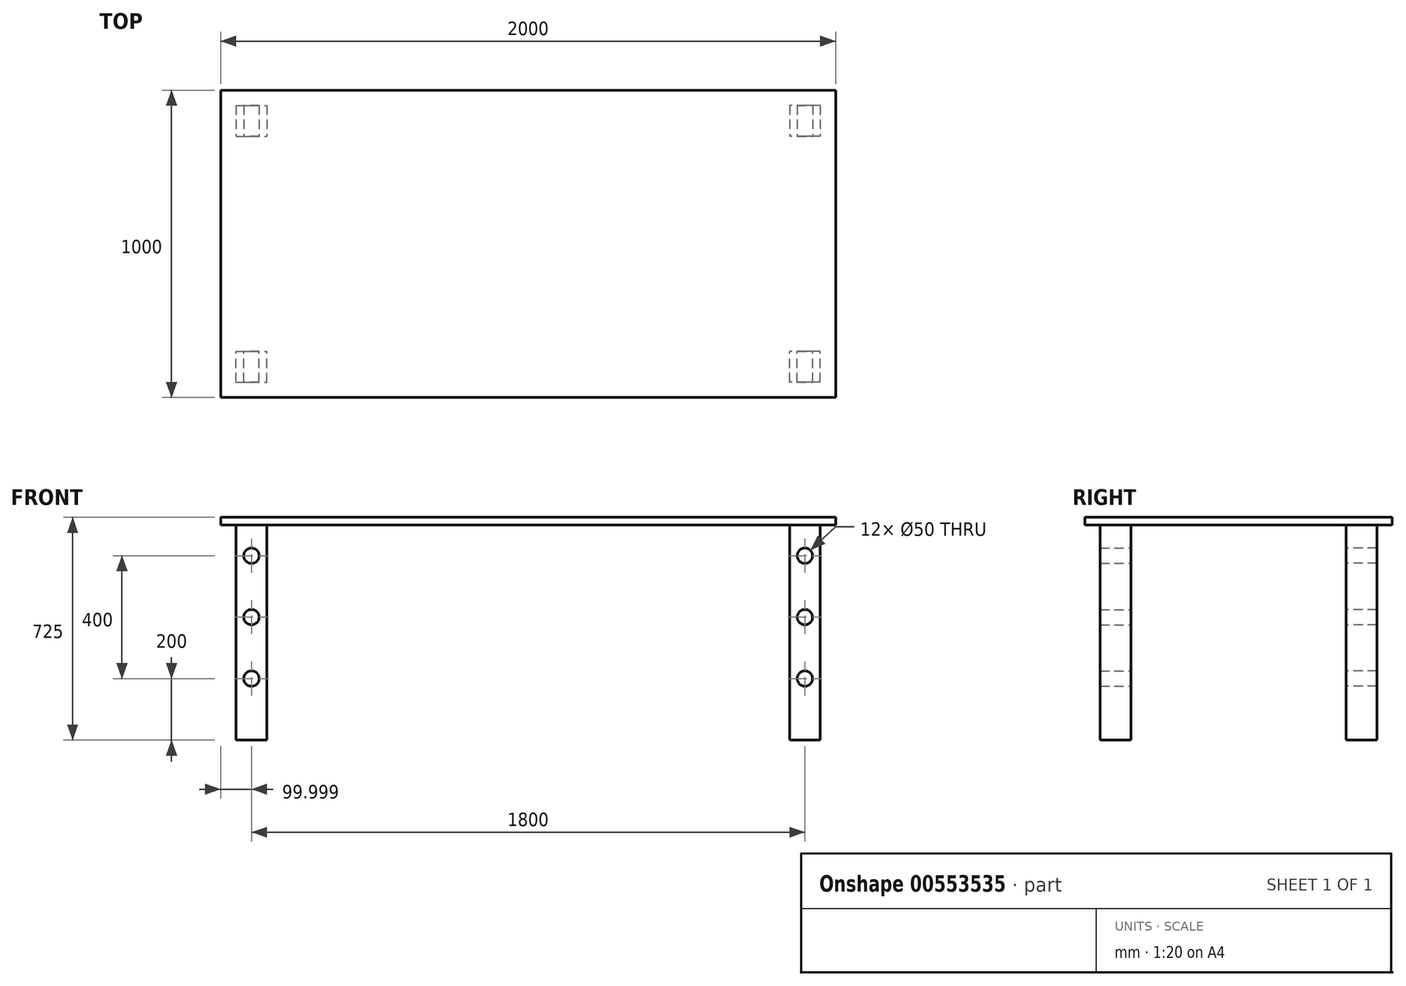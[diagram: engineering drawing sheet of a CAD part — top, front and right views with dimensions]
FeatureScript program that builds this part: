
annotation { "Feature Type Name" : "Feature", "Feature Type Description" : "" }
export const myFeature = defineFeature(function(context is Context, id is Id, definition is map)
    precondition{}
    {
        {
            var Q0;
            Q0=qCreatedBy(makeId("Top.planeOp"),FACE);
            var sketch = newSketch(context, id + "F0", { "sketchPlane" : qUnion([Q0])});
            skLineSegment(sketch, "E0.bottom", {"start": v(-581.73, 260.2) * mm, "end": v(418.27, 260.2) * mm});
            skLineSegment(sketch, "E0.top", {"start": v(-581.73, -239.8) * mm, "end": v(418.27, -239.8) * mm});
            skLineSegment(sketch, "E0.left", {"start": v(-581.73, 260.2) * mm, "end": v(-581.73, -239.8) * mm});
            skLineSegment(sketch, "E0.right", {"start": v(418.27, 260.2) * mm, "end": v(418.27, -239.8) * mm});
            skLineSegment(sketch, "E1.bottom", {"start": v(-531.73, 210.2) * mm, "end": v(-431.73, 210.2) * mm});
            skLineSegment(sketch, "E1.top", {"start": v(-531.73, 110.2) * mm, "end": v(-431.73, 110.2) * mm});
            skLineSegment(sketch, "E1.left", {"start": v(-531.73, 210.2) * mm, "end": v(-531.73, 110.2) * mm});
            skLineSegment(sketch, "E1.right", {"start": v(-431.73, 210.2) * mm, "end": v(-431.73, 110.2) * mm});
            skSolve(sketch);
        }
        {
            var Q0;
            Q0=makeQuery(id+"F0.imprint","IMPRINT",FACE,{"disambiguationData":[TD([[makeQuery(id+"F0.imprint","IMPRINT",EDGE,{"derivedFrom":sQuery(id+"F0.wireOp",EDGE,"E1.bottom")}),-1.0]])]});
            var Q1;
            Q1=makeQuery(id+"F0.imprint","IMPRINT",FACE,{"disambiguationData":[TD([[makeQuery(id+"F0.imprint","IMPRINT",EDGE,{"derivedFrom":sQuery(id+"F0.wireOp",EDGE,"E0.bottom")}),-1.0]])]});
            extrude(context, id + "F1", {"entities" : qUnion([Q0, Q1]), "depth" : 25 * mm, "offsetDistance" : 25 * mm});
        }
        {
            var Q0;
            Q0=makeQuery(id+"F0.imprint","IMPRINT",FACE,{"disambiguationData":[TD([[makeQuery(id+"F0.imprint","IMPRINT",EDGE,{"derivedFrom":sQuery(id+"F0.wireOp",EDGE,"E1.bottom")}),-1.0]])]});
            extrude(context, id + "F2", {"entities" : qUnion([Q0]), "oppositeDirection" : true, "depth" : 700 * mm, "offsetDistance" : 25 * mm});
        }
        {
            var Q0;
            Q0=qCreatedBy(makeId("Front.planeOp"),FACE);
            var sketch = newSketch(context, id + "F3", { "sketchPlane" : qUnion([Q0])});
            skCircle(sketch, "E2", {"center": v(-481.73, -500) * mm, "radius": 25 * mm});
            skCircle(sketch, "E3", {"center": v(-481.73, -300) * mm, "radius": 25 * mm});
            skCircle(sketch, "E4", {"center": v(-481.73, -100) * mm, "radius": 25 * mm});
            skSolve(sketch);
        }
        {
            var Q0;
            Q0=sQuery(id+"F3.wireOp",VERTEX,"E4.center");
            var Q1;
            Q1=sQuery(id+"F3.wireOp",VERTEX,"E3.center");
            var Q2;
            Q2=sQuery(id+"F3.wireOp",VERTEX,"E2.center");
            var Q3;
            Q3=makeQuery(id+"F2.opExtrude","SWEPT_BODY",BODY,{"disambiguationData":[OSD([sQuery(id+"F0.wireOp",EDGE,"E1.bottom"),sQuery(id+"F0.wireOp",EDGE,"E1.top"),sQuery(id+"F0.wireOp",EDGE,"E1.left"),sQuery(id+"F0.wireOp",EDGE,"E1.right")])]});
            hole(context, id + "F4", {"style" : HoleStyle.SIMPLE, "endStyle" : HoleEndStyle.THROUGH, "holeDiameter" : 50 * mm, "isTappedThrough" : true, "tappedDepth" : 12 * mm, "tapClearance" : 3, "locations" : qUnion([Q0, Q1, Q2]), "scope" : qUnion([Q3])});
        }
        {
            var Q0;
            Q0=makeQuery(id+"F1.opExtrude","SWEPT_BODY",BODY,{"disambiguationData":[OSD([sQuery(id+"F0.wireOp",EDGE,"E0.bottom"),sQuery(id+"F0.wireOp",EDGE,"E0.top"),sQuery(id+"F0.wireOp",EDGE,"E0.left"),sQuery(id+"F0.wireOp",EDGE,"E0.right")])]});
            var Q1;
            Q1=makeQuery(id+"F2.opExtrude","SWEPT_BODY",BODY,{"disambiguationData":[OSD([sQuery(id+"F0.wireOp",EDGE,"E1.bottom"),sQuery(id+"F0.wireOp",EDGE,"E1.top"),sQuery(id+"F0.wireOp",EDGE,"E1.left"),sQuery(id+"F0.wireOp",EDGE,"E1.right")])]});
            var Q2;
            Q2=makeQuery(id+"F1.opExtrude","SWEPT_FACE",FACE,{"disambiguationData":[OSD([sQuery(id+"F0.wireOp",EDGE,"E0.top")])]});
            mirror(context, id + "F5", {"operationType" : NewBodyOperationType.ADD, "entities" : qUnion([Q0, Q1]), "mirrorPlane" : qUnion([Q2])});
        }
        {
            var Q0;
            Q0=makeQuery(id+"F1.opExtrude","SWEPT_BODY",BODY,{"disambiguationData":[OSD([sQuery(id+"F0.wireOp",EDGE,"E0.bottom"),sQuery(id+"F0.wireOp",EDGE,"E0.top"),sQuery(id+"F0.wireOp",EDGE,"E0.left"),sQuery(id+"F0.wireOp",EDGE,"E0.right")])]});
            var Q1;
            Q1=makeQuery(id+"F2.opExtrude","SWEPT_BODY",BODY,{"disambiguationData":[OSD([sQuery(id+"F0.wireOp",EDGE,"E1.bottom"),sQuery(id+"F0.wireOp",EDGE,"E1.top"),sQuery(id+"F0.wireOp",EDGE,"E1.left"),sQuery(id+"F0.wireOp",EDGE,"E1.right")])]});
            var Q2;
            {var subQ0=makeQuery(id+"F1.opExtrude","SWEPT_FACE",FACE,{"disambiguationData":[OSD([sQuery(id+"F0.wireOp",EDGE,"E0.right")])]});Q2=makeQuery(id+"F5.boolean.opBoolean","MERGE",FACE,{"derivedFrom":[subQ0,makeQuery(id+"F5.opPattern","COPY",FACE,{"derivedFrom":subQ0,"instanceName":"1"})]});}
            mirror(context, id + "F6", {"operationType" : NewBodyOperationType.ADD, "entities" : qUnion([Q0, Q1]), "mirrorPlane" : qUnion([Q2])});
        }
    });
